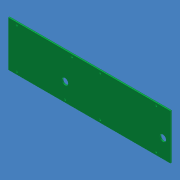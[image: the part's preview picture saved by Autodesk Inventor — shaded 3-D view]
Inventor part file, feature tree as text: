
AUTODESK INVENTOR PART (.ipt)
format: ipt  version: unknown  size: 198,144 bytes
history: native  units: mm (DEFAULTED — no unit token found)
features: sketch x3, hole x2, extrude x1
ambient origin geometry x8: Origin, YZ Plane, XZ Plane, XY Plane, X Axis, Y Axis, Z Axis, Center Point
feature tree (6):
  extrude  "PCB"  Depth=76.2mm
  hole  "Hole1"  [1 undecoded]
  hole  "Hole2"  [1 undecoded]
  sketch  "Sketch1"  dims[d0=273.05mm d1=76.2mm]
  sketch  "Sketch2"  dims[d2=2.2098mm d3=0.0mm d4=67.8434mm]
  sketch  "Sketch3"  dims[d5=14.0208mm d6=93.0148mm d7=47.5742mm d8=94.488mm d9=81.534mm d10=3.429mm d11=12.7mm d12=9.525mm d13=6.35mm d14=14.3117mm d15=19.05mm d16=20.594885mm d17=165.1mm d18=26.2636mm d19=59.055mm d20=11.0744mm d21=12.7mm d22=9.525mm d23=6.35mm d24=14.3117mm d25=19.05mm d26=20.594885mm]
note: 2 required parameter values undecoded (feature->parameter linkage not recoverable at this tier; creation-order binding heuristic only, values carry confidence <= 0.55)
